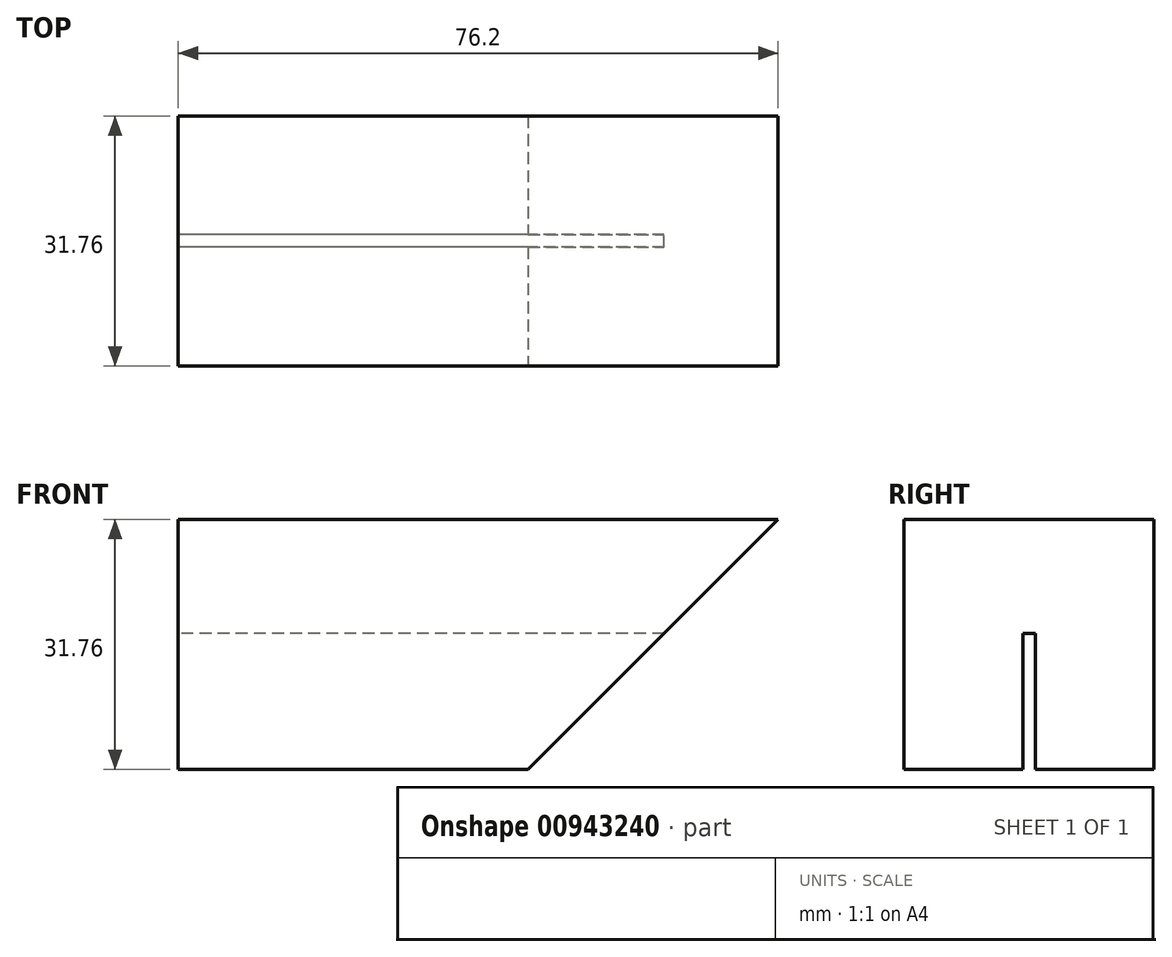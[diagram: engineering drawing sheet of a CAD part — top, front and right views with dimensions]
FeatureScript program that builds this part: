
annotation { "Feature Type Name" : "Feature", "Feature Type Description" : "" }
export const myFeature = defineFeature(function(context is Context, id is Id, definition is map)
    precondition{}
    {
        {
            var Q0;
            Q0=qCreatedBy(makeId("Right.planeOp"),FACE);
            var sketch = newSketch(context, id + "F0", { "sketchPlane" : qUnion([Q0])});
            skLineSegment(sketch, "E0.bottom", {"start": v(-15.87, 15.87) * mm, "end": v(15.88, 15.87) * mm});
            skLineSegment(sketch, "E0.top", {"start": v(-15.87, -15.88) * mm, "end": v(-0.8, -15.88) * mm});
            skLineSegment(sketch, "E0.left", {"start": v(-15.87, 15.87) * mm, "end": v(-15.87, -15.88) * mm});
            skLineSegment(sketch, "E0.right", {"start": v(15.88, 15.87) * mm, "end": v(15.88, -15.88) * mm});
            skLineSegment(sketch, "E1.top", {"start": v(-0.8, 1.4) * mm, "end": v(0.8, 1.4) * mm});
            skLineSegment(sketch, "E1.left", {"start": v(-0.8, -15.87) * mm, "end": v(-0.8, 1.4) * mm});
            skLineSegment(sketch, "E1.right", {"start": v(0.8, -15.87) * mm, "end": v(0.8, 1.4) * mm});
            skLineSegment(sketch, "E2", {"start": v(-15.87, -15.88) * mm, "end": v(15.87, 15.88) * mm, "construction": true});
            skLineSegment(sketch, "E3.trimOffspring", {"start": v(0.8, -15.88) * mm, "end": v(15.88, -15.88) * mm});
            skSolve(sketch);
        }
        {
            var Q0;
            Q0 = qSketchRegion(id + "F0", true);
            extrude(context, id + "F1", {"entities" : qUnion([Q0]), "depth" : 76.2 * mm, "offsetDistance" : 25.4 * mm});
        }
        {
            var Q0;
            Q0=makeQuery(id+"F1.opExtrude","SWEPT_FACE",FACE,{"disambiguationData":[OSD([sQuery(id+"F0.wireOp",EDGE,"E0.left")])]});
            var sketch = newSketch(context, id + "F2", { "sketchPlane" : qUnion([Q0])});
            skLineSegment(sketch, "E4", {"start": v(76.2, 15.87) * mm, "end": v(76.2, -15.88) * mm});
            skLineSegment(sketch, "E5", {"start": v(76.2, -15.88) * mm, "end": v(44.45, -15.88) * mm});
            skLineSegment(sketch, "E6", {"start": v(44.45, -15.88) * mm, "end": v(76.2, 15.88) * mm});
            skSolve(sketch);
        }
        {
            var Q0;
            Q0 = qSketchRegion(id + "F2", true);
            extrude(context, id + "F3", {"entities" : qUnion([Q0]), "operationType" : NewBodyOperationType.REMOVE, "endBound" : BoundingType.THROUGH_ALL, "oppositeDirection" : true, "depth" : 25.4 * mm, "offsetDistance" : 25.4 * mm});
        }
    });
